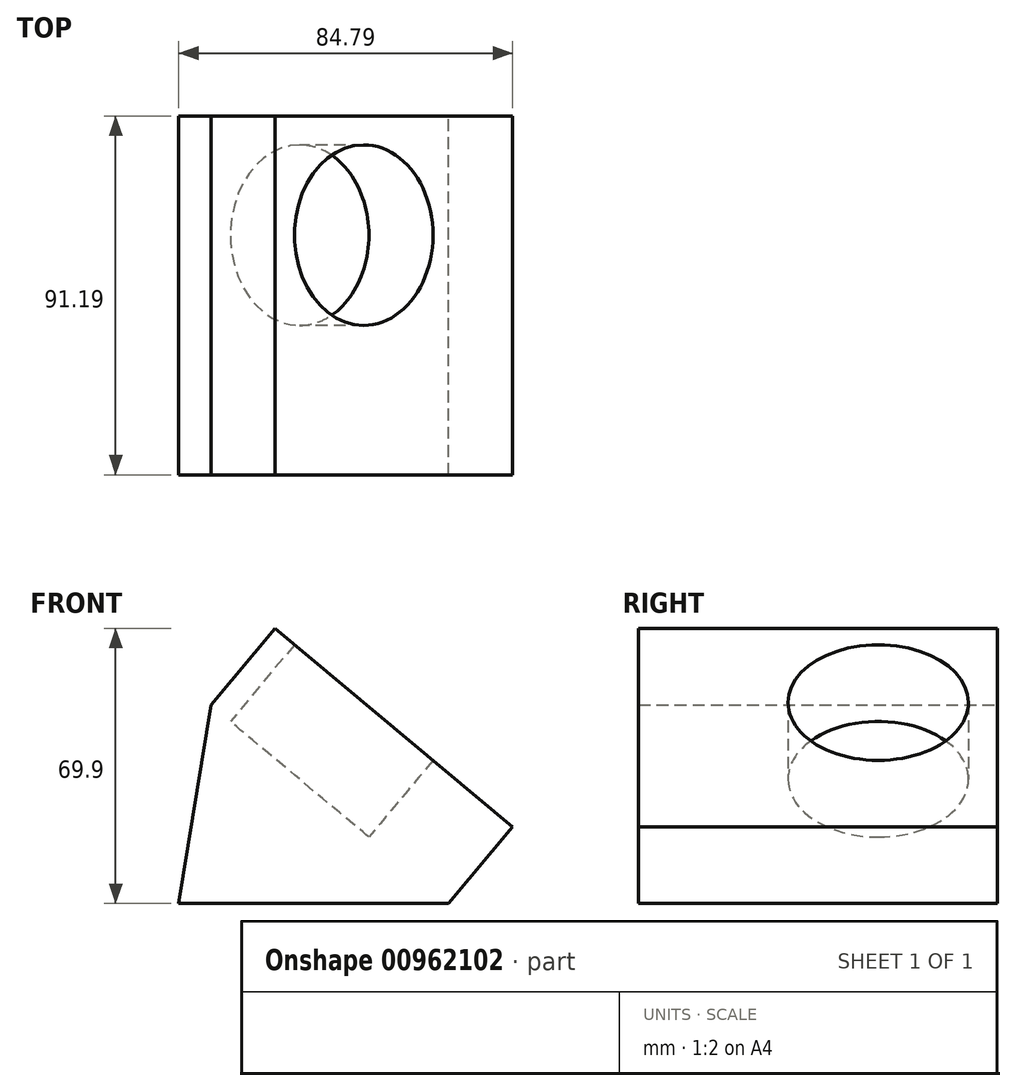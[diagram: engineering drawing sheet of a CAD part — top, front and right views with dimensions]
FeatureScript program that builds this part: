
annotation { "Feature Type Name" : "Feature", "Feature Type Description" : "" }
export const myFeature = defineFeature(function(context is Context, id is Id, definition is map)
    precondition{}
    {
        {
            var Q0;
            Q0=qCreatedBy(makeId("Front.planeOp"),FACE);
            var sketch = newSketch(context, id + "F0", { "sketchPlane" : qUnion([Q0])});
            skLineSegment(sketch, "E0", {"start": v(0, 0) * mm, "end": v(8.14, 50.4) * mm});
            skLineSegment(sketch, "E1", {"start": v(8.14, 50.4) * mm, "end": v(68.51, 0) * mm});
            skLineSegment(sketch, "E2", {"start": v(68.51, 0) * mm, "end": v(0, 0) * mm});
            skSolve(sketch);
        }
        {
            var Q0;
            Q0 = qSketchRegion(id + "F0", true);
            var Q1;
            Q1=makeQuery(id+"F0.imprint","IMPRINT",FACE,{"disambiguationData":[TD([[makeQuery(id+"F0.imprint","IMPRINT",EDGE,{"derivedFrom":sQuery(id+"F0.wireOp",EDGE,"E0")}),-1.0]])]});
            extrude(context, id + "F1", {"entities" : qUnion([Q0, Q1]), "depth" : 91.19 * mm, "offsetDistance" : 25.4 * mm});
        }
        {
            var Q0;
            Q0=makeQuery(id+"F1.opExtrude","SWEPT_FACE",FACE,{"disambiguationData":[OSD([sQuery(id+"F0.wireOp",EDGE,"E1")])]});
            var sketch = newSketch(context, id + "F2", { "sketchPlane" : qUnion([Q0])});
            skCircle(sketch, "E3", {"center": v(3.34, -30.28) * mm, "radius": 22.92 * mm});
            skSolve(sketch);
        }
        {
            var Q0;
            Q0=makeQuery(id+"F2.imprint","IMPRINT",FACE,{"disambiguationData":[TD([[makeQuery(id+"F2.imprint","IMPRINT",EDGE,{"derivedFrom":sQuery(id+"F2.wireOp",EDGE,"E3")}),-1.0]])]});
            extrude(context, id + "F3", {"entities" : qUnion([Q0]), "operationType" : NewBodyOperationType.ADD, "depth" : 25.4 * mm, "offsetDistance" : 25.4 * mm});
        }
    });
